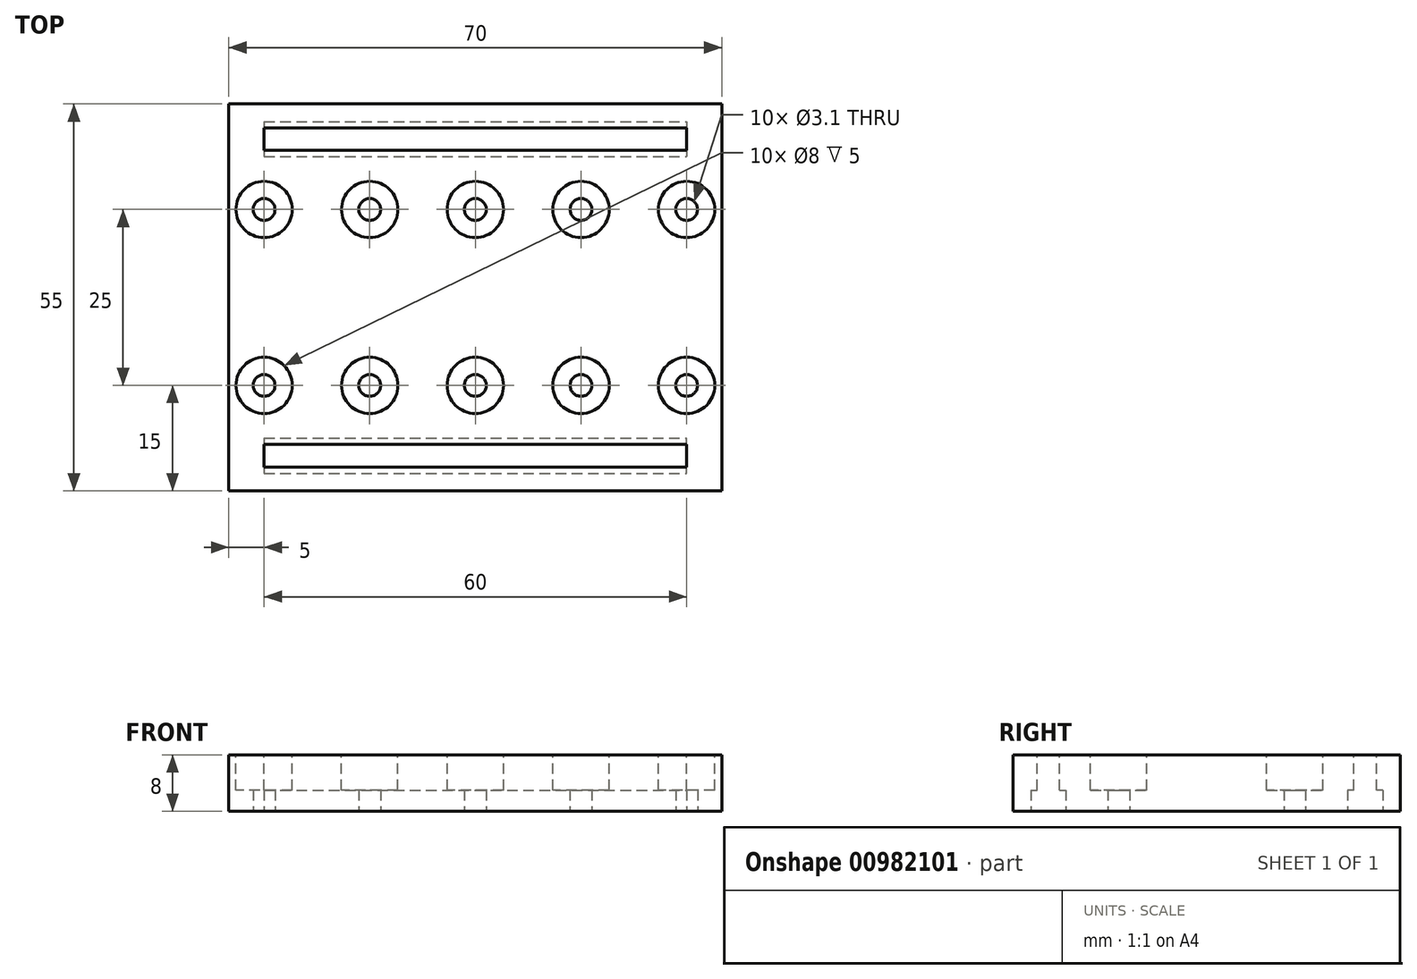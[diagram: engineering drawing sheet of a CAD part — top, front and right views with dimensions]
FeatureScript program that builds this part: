
annotation { "Feature Type Name" : "Feature", "Feature Type Description" : "" }
export const myFeature = defineFeature(function(context is Context, id is Id, definition is map)
    precondition{}
    {
        {
            var Q0;
            Q0=qCreatedBy(makeId("Top.planeOp"),FACE);
            var sketch = newSketch(context, id + "F0", { "sketchPlane" : qUnion([Q0])});
            skPoint(sketch, "E0.middle", {"position": v(0, 0) * mm});
            skLineSegment(sketch, "E1.bottom", {"start": v(-25, 12.5) * mm, "end": v(25, 12.5) * mm, "construction": true});
            skLineSegment(sketch, "E2.bottom", {"start": v(-35, -27.5) * mm, "end": v(35, -27.5) * mm});
            skLineSegment(sketch, "E2.top", {"start": v(-35, 27.5) * mm, "end": v(35, 27.5) * mm});
            skLineSegment(sketch, "E2.left", {"start": v(-35, -27.5) * mm, "end": v(-35, 27.5) * mm});
            skLineSegment(sketch, "E2.right", {"start": v(35, -27.5) * mm, "end": v(35, 27.5) * mm});
            skLineSegment(sketch, "E3", {"start": v(-25, -12.5) * mm, "end": v(25, -12.5) * mm, "construction": true});
            skCircle(sketch, "E4", {"center": v(0, -12.5) * mm, "radius": 1.55 * mm});
            skCircle(sketch, "E5", {"center": v(0, 12.5) * mm, "radius": 1.55 * mm});
            skCircle(sketch, "E6.1.0.0", {"center": v(15, -12.5) * mm, "radius": 1.55 * mm});
            skCircle(sketch, "E6.2.0.0", {"center": v(30, -12.5) * mm, "radius": 1.55 * mm});
            skLineSegment(sketch, "E6.direction1", {"start": v(0, -12.5) * mm, "end": v(15, -12.5) * mm, "construction": true});
            skCircle(sketch, "E7.1.0.0", {"center": v(-15, 12.5) * mm, "radius": 1.55 * mm});
            skCircle(sketch, "E7.2.0.0", {"center": v(-30, 12.5) * mm, "radius": 1.55 * mm});
            skLineSegment(sketch, "E7.direction1", {"start": v(0, 12.5) * mm, "end": v(-15, 12.5) * mm, "construction": true});
            skCircle(sketch, "E8.1.0.0", {"center": v(-15, -12.5) * mm, "radius": 1.55 * mm});
            skCircle(sketch, "E8.2.0.0", {"center": v(-30, -12.5) * mm, "radius": 1.55 * mm});
            skLineSegment(sketch, "E8.direction1", {"start": v(0, -12.5) * mm, "end": v(-15, -12.5) * mm, "construction": true});
            skCircle(sketch, "E9.1.0.0", {"center": v(15, 12.5) * mm, "radius": 1.55 * mm});
            skCircle(sketch, "E9.2.0.0", {"center": v(30, 12.5) * mm, "radius": 1.55 * mm});
            skLineSegment(sketch, "E9.direction1", {"start": v(0, 12.5) * mm, "end": v(15, 12.5) * mm, "construction": true});
            skSolve(sketch);
        }
        {
            var Q0;
            Q0=makeQuery(id+"F0.imprint","IMPRINT",FACE,{"disambiguationData":[TD([[makeQuery(id+"F0.imprint","IMPRINT",EDGE,{"derivedFrom":sQuery(id+"F0.wireOp",EDGE,"E2.bottom")}),1.0]])]});
            extrude(context, id + "F1", {"entities" : qUnion([Q0]), "depth" : 8 * mm, "offsetDistance" : 25 * mm});
        }
        {
            var Q0;
            Q0=makeQuery(id+"F1.opExtrude","CAP_FACE",FACE,{"disambiguationData":[OSD([sQuery(id+"F0.wireOp",EDGE,"E2.bottom"),sQuery(id+"F0.wireOp",EDGE,"E2.top"),sQuery(id+"F0.wireOp",EDGE,"E2.left"),sQuery(id+"F0.wireOp",EDGE,"E2.right"),sQuery(id+"F0.wireOp",EDGE,"E4"),sQuery(id+"F0.wireOp",EDGE,"E5")])],"isStart":false});
            var sketch = newSketch(context, id + "F2", { "sketchPlane" : qUnion([Q0])});
            skCircle(sketch, "E10", {"center": v(0, -12.5) * mm, "radius": 4 * mm});
            skCircle(sketch, "E11.MirrorC", {"center": v(0, 12.5) * mm, "radius": 4 * mm});
            skCircle(sketch, "E12.1.0.0", {"center": v(15, -12.5) * mm, "radius": 4 * mm});
            skCircle(sketch, "E12.2.0.0", {"center": v(30, -12.5) * mm, "radius": 4 * mm});
            skLineSegment(sketch, "E12.direction1", {"start": v(0, -12.5) * mm, "end": v(15, -12.5) * mm, "construction": true});
            skCircle(sketch, "E13.1.0.0", {"center": v(-15, -12.5) * mm, "radius": 4 * mm});
            skCircle(sketch, "E13.2.0.0", {"center": v(-30, -12.5) * mm, "radius": 4 * mm});
            skLineSegment(sketch, "E13.direction1", {"start": v(0, -12.5) * mm, "end": v(-15, -12.5) * mm, "construction": true});
            skCircle(sketch, "E14.1.0.0", {"center": v(15, 12.5) * mm, "radius": 4 * mm});
            skCircle(sketch, "E14.2.0.0", {"center": v(30, 12.5) * mm, "radius": 4 * mm});
            skLineSegment(sketch, "E14.direction1", {"start": v(0, 12.5) * mm, "end": v(15, 12.5) * mm, "construction": true});
            skCircle(sketch, "E15.1.0.0", {"center": v(-15, 12.5) * mm, "radius": 4 * mm});
            skCircle(sketch, "E15.2.0.0", {"center": v(-30, 12.5) * mm, "radius": 4 * mm});
            skLineSegment(sketch, "E15.direction1", {"start": v(0, 12.5) * mm, "end": v(-15, 12.5) * mm, "construction": true});
            skSolve(sketch);
        }
        {
            var Q0;
            Q0 = qSketchRegion(id + "F2", true);
            extrude(context, id + "F3", {"entities" : qUnion([Q0]), "operationType" : NewBodyOperationType.REMOVE, "oppositeDirection" : true, "depth" : 5 * mm, "offsetDistance" : 25 * mm});
        }
        {
            var Q0;
            Q0=makeQuery(id+"F1.opExtrude","CAP_FACE",FACE,{"disambiguationData":[OSD([sQuery(id+"F0.wireOp",EDGE,"E2.bottom"),sQuery(id+"F0.wireOp",EDGE,"E2.top"),sQuery(id+"F0.wireOp",EDGE,"E2.left"),sQuery(id+"F0.wireOp",EDGE,"E2.right"),sQuery(id+"F0.wireOp",EDGE,"E4"),sQuery(id+"F0.wireOp",EDGE,"E5")])],"isStart":false});
            var sketch = newSketch(context, id + "F4", { "sketchPlane" : qUnion([Q0])});
            skLineSegment(sketch, "E16", {"start": v(-35, -27.5) * mm, "end": v(-35, -22.5) * mm});
            skLineSegment(sketch, "E17", {"start": v(-35, -22.5) * mm, "end": v(-30, -22.5) * mm});
            skLineSegment(sketch, "E18", {"start": v(35, -27.5) * mm, "end": v(35, -22.5) * mm});
            skLineSegment(sketch, "E19", {"start": v(35, -22.5) * mm, "end": v(30, -22.5) * mm});
            skLineSegment(sketch, "E20.bottom", {"start": v(30, -22.5) * mm, "end": v(-30, -22.5) * mm});
            skLineSegment(sketch, "E20.top", {"start": v(30, -20) * mm, "end": v(-30, -20) * mm});
            skLineSegment(sketch, "E20.left", {"start": v(30, -22.5) * mm, "end": v(30, -20) * mm});
            skLineSegment(sketch, "E20.right", {"start": v(-30, -22.5) * mm, "end": v(-30, -20) * mm});
            skLineSegment(sketch, "E21.bottom", {"start": v(-30, -22.5) * mm, "end": v(30, -22.5) * mm});
            skLineSegment(sketch, "E21.top", {"start": v(-30, -24.1) * mm, "end": v(30, -24.1) * mm});
            skLineSegment(sketch, "E21.left", {"start": v(-30, -22.5) * mm, "end": v(-30, -24.1) * mm});
            skLineSegment(sketch, "E21.right", {"start": v(30, -22.5) * mm, "end": v(30, -24.1) * mm});
            skLineSegment(sketch, "E22.MirrorCS", {"start": v(-30, -20.9) * mm, "end": v(30, -20.9) * mm});
            skLineSegment(sketch, "E23.MirrorCS", {"start": v(30, -25) * mm, "end": v(-30, -25) * mm});
            skLineSegment(sketch, "E24.MirrorCS", {"start": v(-30, -22.5) * mm, "end": v(-30, -25) * mm});
            skLineSegment(sketch, "E25.MirrorCS", {"start": v(30, -22.5) * mm, "end": v(30, -25) * mm});
            skLineSegment(sketch, "E26.MirrorCS", {"start": v(30, 22.5) * mm, "end": v(-30, 22.5) * mm});
            skLineSegment(sketch, "E27.MirrorCS", {"start": v(-30, 20.9) * mm, "end": v(30, 20.9) * mm});
            skLineSegment(sketch, "E28.MirrorCS", {"start": v(30, 20) * mm, "end": v(-30, 20) * mm});
            skLineSegment(sketch, "E29.MirrorCS", {"start": v(-30, 24.1) * mm, "end": v(30, 24.1) * mm});
            skLineSegment(sketch, "E30.MirrorCS", {"start": v(30, 25) * mm, "end": v(-30, 25) * mm});
            skLineSegment(sketch, "E31.MirrorCS", {"start": v(30, 22.5) * mm, "end": v(30, 25) * mm});
            skLineSegment(sketch, "E32.MirrorCS", {"start": v(30, 22.5) * mm, "end": v(30, 20) * mm});
            skLineSegment(sketch, "E33.MirrorCS", {"start": v(-30, 22.5) * mm, "end": v(-30, 25) * mm});
            skLineSegment(sketch, "E34.MirrorCS", {"start": v(-30, 22.5) * mm, "end": v(-30, 20) * mm});
            skSolve(sketch);
        }
        {
            var Q0;
            {var subQ0=sQuery(id+"F4.wireOp",EDGE,"E20.bottom");Q0=makeQuery(id+"F4.imprint","IMPRINT",FACE,{"disambiguationData":[TD([[makeQuery(id+"F4.imprint","IMPRINT",EDGE,{"derivedFrom":subQ0}),-1.0]])]});}
            var Q1;
            Q1=makeQuery(id+"F4.imprint","IMPRINT",FACE,{"disambiguationData":[TD([[makeQuery(id+"F4.imprint","IMPRINT",EDGE,{"derivedFrom":sQuery(id+"F4.wireOp",EDGE,"E20.bottom")}),1.0]])]});
            var Q2;
            {var subQ0=sQuery(id+"F4.wireOp",EDGE,"E26.MirrorCS");Q2=makeQuery(id+"F4.imprint","IMPRINT",FACE,{"disambiguationData":[TD([[makeQuery(id+"F4.imprint","IMPRINT",EDGE,{"derivedFrom":subQ0}),1.0]])]});}
            var Q3;
            {var subQ0=sQuery(id+"F4.wireOp",EDGE,"E26.MirrorCS");Q3=makeQuery(id+"F4.imprint","IMPRINT",FACE,{"disambiguationData":[TD([[makeQuery(id+"F4.imprint","IMPRINT",EDGE,{"derivedFrom":subQ0}),-1.0]])]});}
            extrude(context, id + "F5", {"entities" : qUnion([Q0, Q1, Q2, Q3]), "operationType" : NewBodyOperationType.REMOVE, "oppositeDirection" : true, "depth" : 5 * mm, "offsetDistance" : 25 * mm});
        }
        {
            var Q0;
            Q0=makeQuery(id+"F1.opExtrude","CAP_FACE",FACE,{"disambiguationData":[OSD([sQuery(id+"F0.wireOp",EDGE,"E2.bottom"),sQuery(id+"F0.wireOp",EDGE,"E2.top"),sQuery(id+"F0.wireOp",EDGE,"E2.left"),sQuery(id+"F0.wireOp",EDGE,"E2.right"),sQuery(id+"F0.wireOp",EDGE,"E4"),sQuery(id+"F0.wireOp",EDGE,"E5")])],"isStart":true});
            var sketch = newSketch(context, id + "F6", { "sketchPlane" : qUnion([Q0])});
            skLineSegment(sketch, "E35.bottom", {"start": v(-30, -22.5) * mm, "end": v(30, -22.5) * mm});
            skLineSegment(sketch, "E35.top", {"start": v(-30, -25) * mm, "end": v(30, -25) * mm});
            skLineSegment(sketch, "E35.left", {"start": v(-30, -22.5) * mm, "end": v(-30, -25) * mm});
            skLineSegment(sketch, "E35.right", {"start": v(30, -22.5) * mm, "end": v(30, -25) * mm});
            skLineSegment(sketch, "E36.MirrorCS", {"start": v(-30, -20) * mm, "end": v(30, -20) * mm});
            skLineSegment(sketch, "E37.MirrorCS", {"start": v(30, -22.5) * mm, "end": v(30, -20) * mm});
            skLineSegment(sketch, "E38.MirrorCS", {"start": v(-30, -22.5) * mm, "end": v(-30, -20) * mm});
            skLineSegment(sketch, "E39.MirrorCS", {"start": v(-30, 20) * mm, "end": v(30, 20) * mm});
            skLineSegment(sketch, "E40.MirrorCS", {"start": v(-30, 25) * mm, "end": v(30, 25) * mm});
            skLineSegment(sketch, "E41.MirrorCS", {"start": v(30, 22.5) * mm, "end": v(30, 25) * mm});
            skLineSegment(sketch, "E42.MirrorCS", {"start": v(30, 22.5) * mm, "end": v(30, 20) * mm});
            skLineSegment(sketch, "E43.MirrorCS", {"start": v(-30, 22.5) * mm, "end": v(-30, 25) * mm});
            skLineSegment(sketch, "E44.MirrorCS", {"start": v(-30, 22.5) * mm, "end": v(-30, 20) * mm});
            skSolve(sketch);
        }
        {
            var Q0;
            {var subQ0=sQuery(id+"F6.wireOp",EDGE,"E39.MirrorCS");Q0=makeQuery(id+"F6.imprint","IMPRINT",FACE,{"disambiguationData":[TD([[makeQuery(id+"F6.imprint","IMPRINT",EDGE,{"derivedFrom":subQ0}),1.0]])]});}
            var Q1;
            {var subQ0=sQuery(id+"F6.wireOp",EDGE,"E40.MirrorCS");Q1=makeQuery(id+"F6.imprint","IMPRINT",FACE,{"disambiguationData":[TD([[makeQuery(id+"F6.imprint","IMPRINT",EDGE,{"derivedFrom":subQ0}),-1.0]])]});}
            var Q2;
            {var subQ0=sQuery(id+"F6.wireOp",EDGE,"E36.MirrorCS");Q2=makeQuery(id+"F6.imprint","IMPRINT",FACE,{"disambiguationData":[TD([[makeQuery(id+"F6.imprint","IMPRINT",EDGE,{"derivedFrom":subQ0}),-1.0]])]});}
            var Q3;
            {var subQ0=sQuery(id+"F6.wireOp",EDGE,"E35.top");Q3=makeQuery(id+"F6.imprint","IMPRINT",FACE,{"disambiguationData":[TD([[makeQuery(id+"F6.imprint","IMPRINT",EDGE,{"derivedFrom":subQ0}),1.0]])]});}
            extrude(context, id + "F7", {"entities" : qUnion([Q0, Q1, Q2, Q3]), "operationType" : NewBodyOperationType.REMOVE, "oppositeDirection" : true, "depth" : 3 * mm, "offsetDistance" : 25 * mm});
        }
    });
